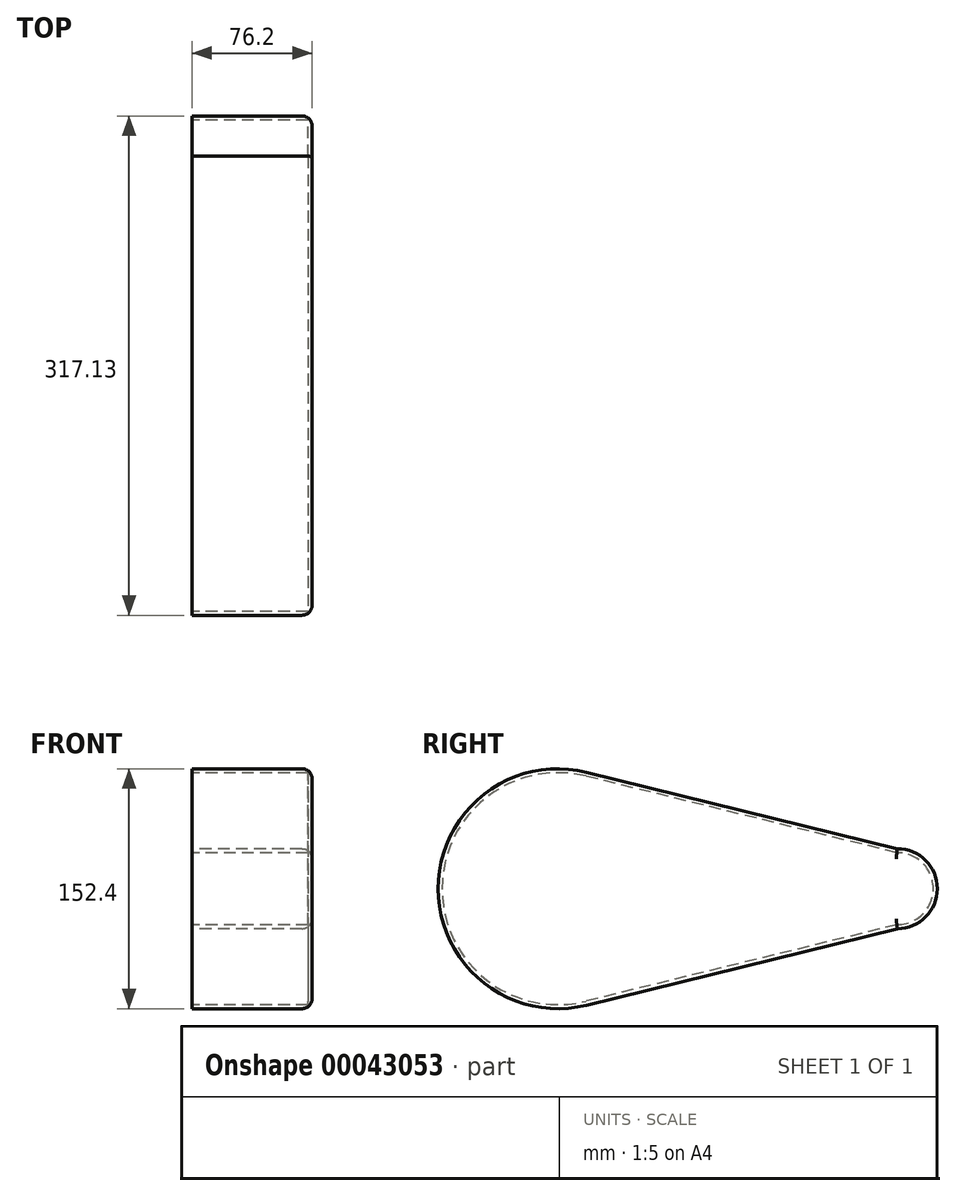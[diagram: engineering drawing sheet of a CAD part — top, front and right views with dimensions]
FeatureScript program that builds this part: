
annotation { "Feature Type Name" : "Feature", "Feature Type Description" : "" }
export const myFeature = defineFeature(function(context is Context, id is Id, definition is map)
    precondition{}
    {
        {
            var Q0;
            Q0=qCreatedBy(makeId("Right.planeOp"),FACE);
            var sketch = newSketch(context, id + "F0", { "sketchPlane" : qUnion([Q0])});
            skCircle(sketch, "E0", {"center": v(-140.27, 0) * mm, "radius": 76.2 * mm});
            skCircle(sketch, "E1", {"center": v(75.26, 0) * mm, "radius": 25.4 * mm});
            skLineSegment(sketch, "E2", {"start": v(75.26, 25.4) * mm, "end": v(-122.05, 73.99) * mm});
            skLineSegment(sketch, "E3", {"start": v(75.26, -25.4) * mm, "end": v(-122.05, -73.99) * mm});
            skSolve(sketch);
        }
        {
            var Q0;
            Q0 = qSketchRegion(id + "F0", true);
            extrude(context, id + "F1", {"entities" : qUnion([Q0]), "depth" : 76.2 * mm});
        }
        {
            var Q0;
            Q0=makeQuery(id+"F1.opExtrude","CAP_FACE",FACE,{"disambiguationData":[OSD([sQuery(id+"F0.wireOp",EDGE,"E0"),sQuery(id+"F0.wireOp",EDGE,"E1"),sQuery(id+"F0.wireOp",EDGE,"E2"),sQuery(id+"F0.wireOp",EDGE,"E3")])],"isStart":false});
            var sketch = newSketch(context, id + "F2", { "sketchPlane" : qUnion([Q0])});
            skCircle(sketch, "E4", {"center": v(-140.27, 0) * mm, "radius": 66.04 * mm});
            skCircle(sketch, "E5", {"center": v(75.26, 0) * mm, "radius": 15.24 * mm});
            skSolve(sketch);
        }
        {
            var Q0;
            Q0=sQuery(id+"F2.wireOp",EDGE,"E4");
            var Q1;
            Q1=sQuery(id+"F2.wireOp",EDGE,"E5");
            extrude(context, id + "F3", {"bodyType" : ToolBodyType.SURFACE, "surfaceEntities" : qUnion([Q0, Q1]), "oppositeDirection" : true, "depth" : 50.8 * mm});
        }
        {
            var Q0;
            Q0=makeQuery(id+"F1.opExtrude","CAP_FACE",FACE,{"disambiguationData":[OSD([sQuery(id+"F0.wireOp",EDGE,"E0"),sQuery(id+"F0.wireOp",EDGE,"E1"),sQuery(id+"F0.wireOp",EDGE,"E2"),sQuery(id+"F0.wireOp",EDGE,"E3")])],"isStart":true});
            shell(context, id + "F4", {"entities" : qUnion([Q0]), "thickness" : 2.54 * mm});
        }
        {
            var Q0;
            Q0=makeQuery(id+"F1.opExtrude","CAP_FACE",FACE,{"disambiguationData":[OSD([sQuery(id+"F0.wireOp",EDGE,"E0"),sQuery(id+"F0.wireOp",EDGE,"E1"),sQuery(id+"F0.wireOp",EDGE,"E2"),sQuery(id+"F0.wireOp",EDGE,"E3")])],"isStart":false});
            fillet(context, id + "F5", {"entities" : qUnion([Q0]), "radius" : 6.35 * mm, "tangentPropagation" : true, "allowEdgeOverflow" : false});
        }
    });
